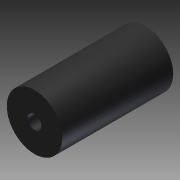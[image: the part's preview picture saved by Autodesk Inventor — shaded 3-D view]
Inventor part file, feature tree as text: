
AUTODESK INVENTOR PART (.ipt)
format: ipt  version: 2012 (Build 160160000, 160)  size: 75,264 bytes
history: native  units: in
note: dims shown in document units (in); Inventor stores cm internally (conversion verified against a paired STEP export)
features: extrude x1, sketch x1
ambient origin geometry x8: Origin, YZ Plane, XZ Plane, XY Plane, X Axis, Y Axis, Z Axis, Center Point
bodies: Solid1 (feature_tree)
feature tree (2):
  extrude  "Extrusion1"  Depth=2.0in
  sketch  "Sketch1"  dims[d0=0.5in d1=2.0in d2=4.0in d3=0.0in]
